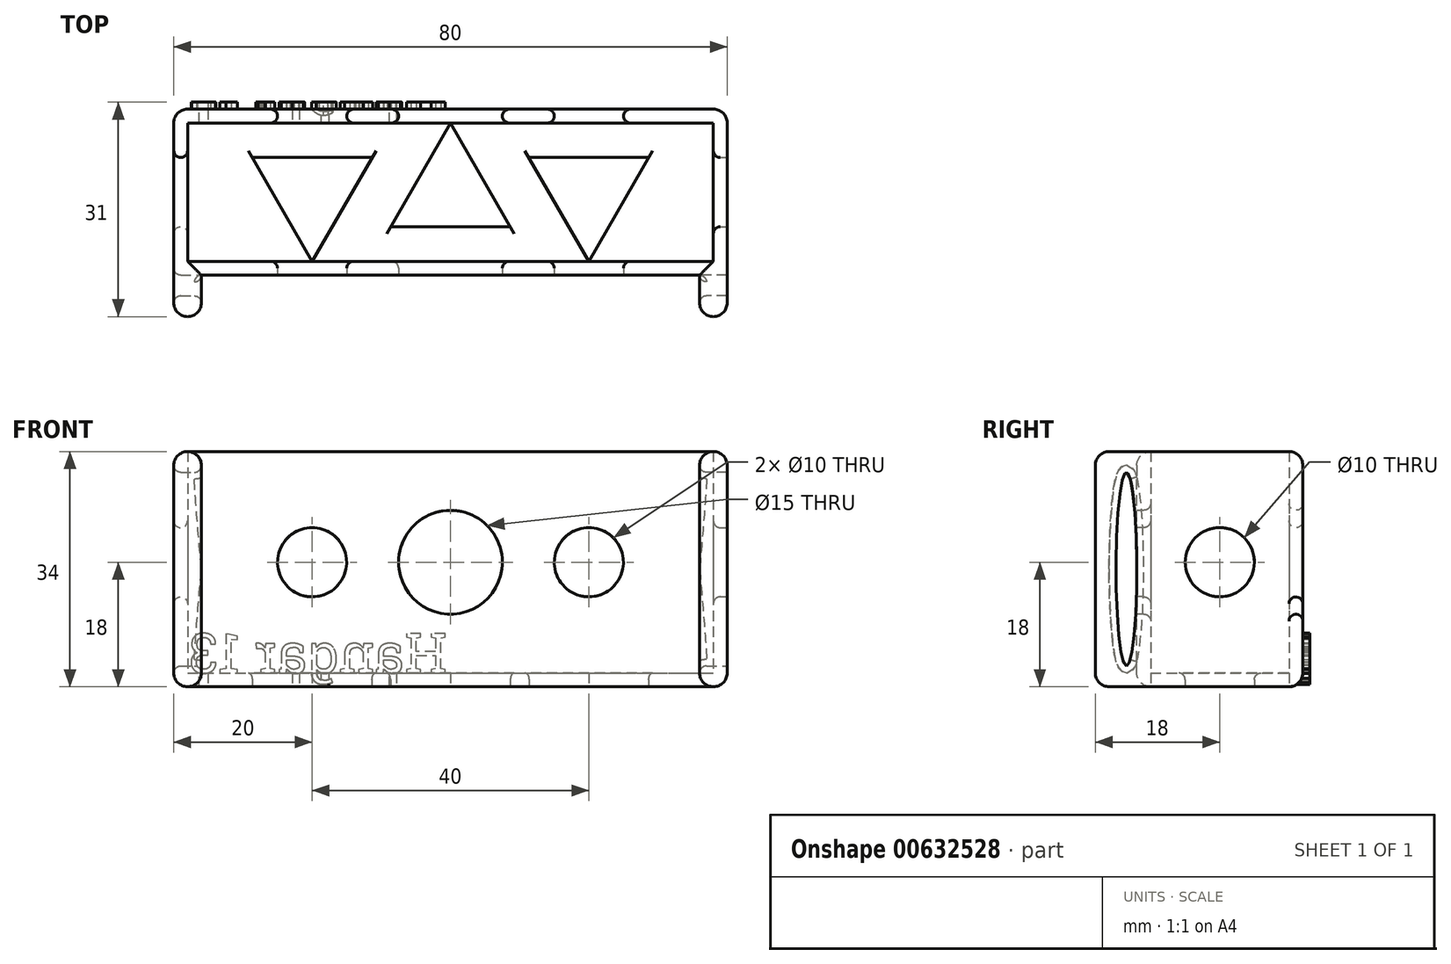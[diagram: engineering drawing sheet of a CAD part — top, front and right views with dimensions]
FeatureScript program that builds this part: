
annotation { "Feature Type Name" : "Feature", "Feature Type Description" : "" }
export const myFeature = defineFeature(function(context is Context, id is Id, definition is map)
    precondition{}
    {
        {
            var Q0;
            Q0=qCreatedBy(makeId("Top.planeOp"),FACE);
            var sketch = newSketch(context, id + "F0", { "sketchPlane" : qUnion([Q0])});
            skLineSegment(sketch, "E0.bottom", {"start": v(0, 0) * mm, "end": v(76, 0) * mm});
            skLineSegment(sketch, "E0.top", {"start": v(0, 20) * mm, "end": v(76, 20) * mm});
            skLineSegment(sketch, "E0.left", {"start": v(0, 0) * mm, "end": v(0, 20) * mm});
            skLineSegment(sketch, "E0.right", {"start": v(76, 0) * mm, "end": v(76, 20) * mm});
            skLineSegment(sketch, "E1.0", {"start": v(-2, -2) * mm, "end": v(78, -2) * mm});
            skLineSegment(sketch, "E1.1", {"start": v(-2, -2) * mm, "end": v(-2, 22) * mm});
            skLineSegment(sketch, "E1.2", {"start": v(-2, 22) * mm, "end": v(78, 22) * mm});
            skLineSegment(sketch, "E1.3", {"start": v(78, -2) * mm, "end": v(78, 22) * mm});
            skSolve(sketch);
        }
        {
            var Q0;
            Q0=makeQuery(id+"F0.imprint","IMPRINT",FACE,{"disambiguationData":[TD([[makeQuery(id+"F0.imprint","IMPRINT",EDGE,{"derivedFrom":sQuery(id+"F0.wireOp",EDGE,"E0.bottom")}),-1.0]])]});
            extrude(context, id + "F1", {"entities" : qUnion([Q0]), "depth" : 32 * mm, "offsetDistance" : 25 * mm});
        }
        {
            var Q0;
            Q0=makeQuery(id+"F1.opExtrude","SWEPT_FACE",FACE,{"disambiguationData":[OSD([sQuery(id+"F0.wireOp",EDGE,"E1.0")])]});
            var sketch = newSketch(context, id + "F2", { "sketchPlane" : qUnion([Q0])});
            skCircle(sketch, "E2", {"center": v(18, 16) * mm, "radius": 5 * mm});
            skCircle(sketch, "E3", {"center": v(38, 16) * mm, "radius": 7.5 * mm});
            skCircle(sketch, "E4", {"center": v(58, 16) * mm, "radius": 5 * mm});
            skSolve(sketch);
        }
        {
            var Q0;
            Q0=makeQuery(id+"F2.imprint","IMPRINT",FACE,{"disambiguationData":[TD([[makeQuery(id+"F2.imprint","IMPRINT",EDGE,{"derivedFrom":sQuery(id+"F2.wireOp",EDGE,"E3")}),1.0]])]});
            var Q1;
            Q1=makeQuery(id+"F2.imprint","IMPRINT",FACE,{"disambiguationData":[TD([[makeQuery(id+"F2.imprint","IMPRINT",EDGE,{"derivedFrom":sQuery(id+"F2.wireOp",EDGE,"E2")}),1.0]])]});
            var Q2;
            Q2=makeQuery(id+"F2.imprint","IMPRINT",FACE,{"disambiguationData":[TD([[makeQuery(id+"F2.imprint","IMPRINT",EDGE,{"derivedFrom":sQuery(id+"F2.wireOp",EDGE,"E4")}),1.0]])]});
            extrude(context, id + "F3", {"entities" : qUnion([Q0, Q1, Q2]), "operationType" : NewBodyOperationType.REMOVE, "oppositeDirection" : true, "depth" : 25 * mm, "offsetDistance" : 25 * mm});
        }
        {
            var Q0;
            Q0=makeQuery(id+"F1.opExtrude","SWEPT_FACE",FACE,{"disambiguationData":[OSD([sQuery(id+"F0.wireOp",EDGE,"E1.3")])]});
            var sketch = newSketch(context, id + "F4", { "sketchPlane" : qUnion([Q0])});
            skCircle(sketch, "E5", {"center": v(10, 16) * mm, "radius": 5 * mm});
            skSolve(sketch);
        }
        {
            var Q0;
            Q0=makeQuery(id+"F4.imprint","IMPRINT",FACE,{"disambiguationData":[TD([[makeQuery(id+"F4.imprint","IMPRINT",EDGE,{"derivedFrom":sQuery(id+"F4.wireOp",EDGE,"E5")}),1.0]])]});
            extrude(context, id + "F5", {"entities" : qUnion([Q0]), "operationType" : NewBodyOperationType.REMOVE, "oppositeDirection" : true, "depth" : 95 * mm, "offsetDistance" : 25 * mm});
        }
        {
            var Q0;
            Q0=makeQuery(id+"F1.opExtrude","CAP_FACE",FACE,{"disambiguationData":[OSD([sQuery(id+"F0.wireOp",EDGE,"E0.bottom"),sQuery(id+"F0.wireOp",EDGE,"E0.top"),sQuery(id+"F0.wireOp",EDGE,"E0.left"),sQuery(id+"F0.wireOp",EDGE,"E0.right"),sQuery(id+"F0.wireOp",EDGE,"E1.0"),sQuery(id+"F0.wireOp",EDGE,"E1.1"),sQuery(id+"F0.wireOp",EDGE,"E1.2"),sQuery(id+"F0.wireOp",EDGE,"E1.3")])],"isStart":true});
            var sketch = newSketch(context, id + "F6", { "sketchPlane" : qUnion([Q0])});
            skLineSegment(sketch, "E6.bottom", {"start": v(-2, 2) * mm, "end": v(78, 2) * mm});
            skLineSegment(sketch, "E6.top", {"start": v(-2, -22) * mm, "end": v(78, -22) * mm});
            skLineSegment(sketch, "E6.left", {"start": v(-2, 2) * mm, "end": v(-2, -22) * mm});
            skLineSegment(sketch, "E6.right", {"start": v(78, 2) * mm, "end": v(78, -22) * mm});
            skSolve(sketch);
        }
        {
            var Q0;
            Q0 = qSketchRegion(id + "F6", true);
            extrude(context, id + "F7", {"entities" : qUnion([Q0]), "operationType" : NewBodyOperationType.ADD, "depth" : 2 * mm, "offsetDistance" : 25 * mm});
        }
        {
            var Q0;
            Q0=makeQuery(id+"F7.boolean.opBoolean","MERGE",FACE,{"derivedFrom":[makeQuery(id+"F1.opExtrude","SWEPT_FACE",FACE,{"disambiguationData":[OSD([sQuery(id+"F0.wireOp",EDGE,"E1.0")])]}),makeQuery(id+"F7.opExtrude","SWEPT_FACE",FACE,{"disambiguationData":[OSD([sQuery(id+"F6.wireOp",EDGE,"E6.bottom")])]})]});
            var sketch = newSketch(context, id + "F8", { "sketchPlane" : qUnion([Q0])});
            skLineSegment(sketch, "E7.bottom", {"start": v(-2, -2) * mm, "end": v(2, -2) * mm});
            skLineSegment(sketch, "E7.top", {"start": v(-2, 32) * mm, "end": v(2, 32) * mm});
            skLineSegment(sketch, "E7.left", {"start": v(-2, -2) * mm, "end": v(-2, 32) * mm});
            skLineSegment(sketch, "E7.right", {"start": v(2, -2) * mm, "end": v(2, 32) * mm});
            skLineSegment(sketch, "E8.bottom", {"start": v(78, 32) * mm, "end": v(74, 32) * mm});
            skLineSegment(sketch, "E8.top", {"start": v(78, -2) * mm, "end": v(74, -2) * mm});
            skLineSegment(sketch, "E8.left", {"start": v(78, 32) * mm, "end": v(78, -2) * mm});
            skLineSegment(sketch, "E8.right", {"start": v(74, 32) * mm, "end": v(74, -2) * mm});
            skSolve(sketch);
        }
        {
            var Q0;
            Q0=makeQuery(id+"F8.imprint","IMPRINT",FACE,{"disambiguationData":[TD([[makeQuery(id+"F8.imprint","IMPRINT",EDGE,{"derivedFrom":sQuery(id+"F8.wireOp",EDGE,"E7.bottom")}),1.0]])]});
            var Q1;
            Q1=makeQuery(id+"F8.imprint","IMPRINT",FACE,{"disambiguationData":[TD([[makeQuery(id+"F8.imprint","IMPRINT",EDGE,{"derivedFrom":sQuery(id+"F8.wireOp",EDGE,"E8.bottom")}),-1.0]])]});
            extrude(context, id + "F9", {"entities" : qUnion([Q0, Q1]), "operationType" : NewBodyOperationType.ADD, "depth" : 6 * mm, "offsetDistance" : 25 * mm});
        }
        {
            var Q0;
            Q0=makeQuery(id+"F9.boolean.opBoolean","MERGE",FACE,{"derivedFrom":[makeQuery(id+"F7.boolean.opBoolean","MERGE",FACE,{"derivedFrom":[makeQuery(id+"F1.opExtrude","SWEPT_FACE",FACE,{"disambiguationData":[OSD([sQuery(id+"F0.wireOp",EDGE,"E1.3")])]}),makeQuery(id+"F7.opExtrude","SWEPT_FACE",FACE,{"disambiguationData":[OSD([sQuery(id+"F6.wireOp",EDGE,"E6.right")])]})]}),makeQuery(id+"F9.opExtrude","SWEPT_FACE",FACE,{"disambiguationData":[OSD([sQuery(id+"F8.wireOp",EDGE,"E8.left")])]})]});
            var sketch = newSketch(context, id + "F10", { "sketchPlane" : qUnion([Q0])});
            skLineSegment(sketch, "E9.bottom", {"start": v(-8, 32) * mm, "end": v(-2, 32) * mm});
            skLineSegment(sketch, "E9.top", {"start": v(-8, -2) * mm, "end": v(-2, -2) * mm});
            skLineSegment(sketch, "E9.left", {"start": v(-8, 32) * mm, "end": v(-8, -2) * mm});
            skEllipse(sketch, "E10", {"center": v(-3.5, 15) * mm, "majorRadius": 14 * mm, "minorRadius": 1.5 * mm, "majorAxis": v(0, -1)});
            skSolve(sketch);
        }
        {
            var Q0;
            Q0 = qSketchRegion(id + "F10", true);
            extrude(context, id + "F11", {"entities" : qUnion([Q0]), "operationType" : NewBodyOperationType.REMOVE, "oppositeDirection" : true, "depth" : 88.9 * mm, "offsetDistance" : 25 * mm});
        }
        {
            var Q0;
            Q0=makeQuery(id+"F9.boolean.opBoolean","MERGE",FACE,{"derivedFrom":[makeQuery(id+"F7.opExtrude","CAP_FACE",FACE,{"disambiguationData":[OSD([sQuery(id+"F6.wireOp",EDGE,"E6.bottom"),sQuery(id+"F6.wireOp",EDGE,"E6.top"),sQuery(id+"F6.wireOp",EDGE,"E6.left"),sQuery(id+"F6.wireOp",EDGE,"E6.right")])],"isStart":false}),makeQuery(id+"F9.opExtrude","SWEPT_FACE",FACE,{"disambiguationData":[OSD([sQuery(id+"F8.wireOp",EDGE,"E7.bottom")])]}),makeQuery(id+"F9.opExtrude","SWEPT_FACE",FACE,{"disambiguationData":[OSD([sQuery(id+"F8.wireOp",EDGE,"E8.top")])]})]});
            var sketch = newSketch(context, id + "F12", { "sketchPlane" : qUnion([Q0])});
            skCircle(sketch, "E11.cCircle", {"center": v(58, -10) * mm, "radius": 10 * mm, "construction": true});
            skPoint(sketch, "E11.cCircle.perimeterSnap0", {"position": v(58, -10) * mm});
            skLineSegment(sketch, "E11.0", {"start": v(58, 0) * mm, "end": v(66.66, -15) * mm});
            skPoint(sketch, "E11.0.startSnap0", {"position": v(58, -10) * mm});
            skLineSegment(sketch, "E11.1", {"start": v(66.66, -15) * mm, "end": v(49.34, -15) * mm});
            skLineSegment(sketch, "E11.2", {"start": v(49.34, -15) * mm, "end": v(58, 0) * mm});
            skCircle(sketch, "E12.cCircle", {"center": v(38, -10) * mm, "radius": 10 * mm, "construction": true});
            skLineSegment(sketch, "E12.0", {"start": v(38, -20) * mm, "end": v(29.34, -5) * mm});
            skLineSegment(sketch, "E12.1", {"start": v(29.34, -5) * mm, "end": v(46.66, -5) * mm});
            skLineSegment(sketch, "E12.2", {"start": v(46.66, -5) * mm, "end": v(38, -20) * mm});
            skCircle(sketch, "E13.cCircle", {"center": v(18, -10) * mm, "radius": 10 * mm, "construction": true});
            skPoint(sketch, "E13.cCircle.perimeterSnap0", {"position": v(18, -10) * mm});
            skLineSegment(sketch, "E13.0", {"start": v(18, 0) * mm, "end": v(26.66, -15) * mm});
            skPoint(sketch, "E13.0.startSnap0", {"position": v(18, -10) * mm});
            skLineSegment(sketch, "E13.1", {"start": v(26.66, -15) * mm, "end": v(9.34, -15) * mm});
            skLineSegment(sketch, "E13.2", {"start": v(9.34, -15) * mm, "end": v(18, 0) * mm});
            skSolve(sketch);
        }
        {
            var Q0;
            Q0=makeQuery(id+"F12.imprint","IMPRINT",FACE,{"disambiguationData":[TD([[makeQuery(id+"F12.imprint","IMPRINT",EDGE,{"derivedFrom":sQuery(id+"F12.wireOp",EDGE,"E12.0")}),-1.0]])]});
            var Q1;
            Q1=makeQuery(id+"F12.imprint","IMPRINT",FACE,{"disambiguationData":[TD([[makeQuery(id+"F12.imprint","IMPRINT",EDGE,{"derivedFrom":sQuery(id+"F12.wireOp",EDGE,"E11.0")}),-1.0]])]});
            var Q2;
            Q2=makeQuery(id+"F12.imprint","IMPRINT",FACE,{"disambiguationData":[TD([[makeQuery(id+"F12.imprint","IMPRINT",EDGE,{"derivedFrom":sQuery(id+"F12.wireOp",EDGE,"E13.0")}),-1.0]])]});
            extrude(context, id + "F13", {"entities" : qUnion([Q0, Q1, Q2]), "operationType" : NewBodyOperationType.REMOVE, "oppositeDirection" : true, "depth" : 25 * mm, "offsetDistance" : 25 * mm});
        }
        {
            var Q0;
            Q0=makeQuery(id+"F7.boolean.opBoolean","MERGE",FACE,{"derivedFrom":[makeQuery(id+"F1.opExtrude","SWEPT_FACE",FACE,{"disambiguationData":[OSD([sQuery(id+"F0.wireOp",EDGE,"E1.2")])]}),makeQuery(id+"F7.opExtrude","SWEPT_FACE",FACE,{"disambiguationData":[OSD([sQuery(id+"F6.wireOp",EDGE,"E6.top")])]})]});
            var sketch = newSketch(context, id + "F14", { "sketchPlane" : qUnion([Q0])});
            skText(sketch, "E14", { "text": "Hangar 13", "fontName": "RobotoSlab-Regular.ttf"});
            const initialGuessF14  = {"E14": [-0.0375, 0, 1, 0, 0.00574]};
            skSetInitialGuess(sketch, initialGuessF14);
            skSolve(sketch);
        }
        {
            var Q0;
            Q0 = qSketchRegion(id + "F14", true);
            extrude(context, id + "F15", {"entities" : qUnion([Q0]), "operationType" : NewBodyOperationType.ADD, "depth" : 1 * mm, "offsetDistance" : 25 * mm});
        }
        {
            var Q0;
            Q0=makeQuery(id+"F7.boolean.opBoolean","MERGE",EDGE,{"derivedFrom":[makeQuery(id+"F1.opExtrude","SWEPT_EDGE",EDGE,{"disambiguationData":[OSD([sQuery(id+"F0.wireOp",EDGE,"E1.1"),sQuery(id+"F0.wireOp",EDGE,"E1.2")])]}),makeQuery(id+"F7.opExtrude","SWEPT_EDGE",EDGE,{"disambiguationData":[OSD([sQuery(id+"F6.wireOp",EDGE,"E6.top"),sQuery(id+"F6.wireOp",EDGE,"E6.left")])]})]});
            var Q1;
            Q1=makeQuery(id+"F7.boolean.opBoolean","MERGE",EDGE,{"derivedFrom":[makeQuery(id+"F1.opExtrude","SWEPT_EDGE",EDGE,{"disambiguationData":[OSD([sQuery(id+"F0.wireOp",EDGE,"E1.2"),sQuery(id+"F0.wireOp",EDGE,"E1.3")])]}),makeQuery(id+"F7.opExtrude","SWEPT_EDGE",EDGE,{"disambiguationData":[OSD([sQuery(id+"F6.wireOp",EDGE,"E6.top"),sQuery(id+"F6.wireOp",EDGE,"E6.right")])]})]});
            var Q2;
            Q2=makeQuery(id+"F9.opExtrude","CAP_EDGE",EDGE,{"disambiguationData":[OSD([sQuery(id+"F8.wireOp",EDGE,"E7.left")])],"isStart":false});
            var Q3;
            Q3=makeQuery(id+"F9.opExtrude","CAP_EDGE",EDGE,{"disambiguationData":[OSD([sQuery(id+"F8.wireOp",EDGE,"E7.right")])],"isStart":false});
            var Q4;
            Q4=makeQuery(id+"F9.opExtrude","CAP_EDGE",EDGE,{"disambiguationData":[OSD([sQuery(id+"F8.wireOp",EDGE,"E8.right")])],"isStart":false});
            var Q5;
            Q5=makeQuery(id+"F9.opExtrude","CAP_EDGE",EDGE,{"disambiguationData":[OSD([sQuery(id+"F8.wireOp",EDGE,"E8.left")])],"isStart":false});
            fillet(context, id + "F16", {"entities" : qUnion([Q0, Q1, Q2, Q3, Q4, Q5]), "radius" : 2 * mm, "tangentPropagation" : true, "allowEdgeOverflow" : false});
        }
        {
            var Q0;
            Q0=makeQuery(id+"F1.opExtrude","CAP_EDGE",EDGE,{"disambiguationData":[OSD([sQuery(id+"F0.wireOp",EDGE,"E1.2")])],"isStart":false});
            var Q1;
            Q1=makeQuery(id+"F7.opExtrude","CAP_EDGE",EDGE,{"disambiguationData":[OSD([sQuery(id+"F6.wireOp",EDGE,"E6.top")])],"isStart":false});
            var Q2;
            Q2=makeQuery(id+"F7.opExtrude","CAP_EDGE",EDGE,{"disambiguationData":[OSD([sQuery(id+"F6.wireOp",EDGE,"E6.bottom")])],"isStart":false});
            var Q3;
            Q3=makeQuery(id+"F1.opExtrude","CAP_EDGE",EDGE,{"disambiguationData":[OSD([sQuery(id+"F0.wireOp",EDGE,"E1.0")])],"isStart":false});
            fillet(context, id + "F17", {"entities" : qUnion([Q0, Q1, Q2, Q3]), "radius" : 2 * mm, "tangentPropagation" : true, "allowEdgeOverflow" : false});
        }
        {
            var Q0;
            Q0=makeQuery(id+"F3.boolean.opBoolean","INTERSECT",EDGE,{"derivedFrom":[makeQuery(id+"F1.opExtrude","SWEPT_FACE",FACE,{"disambiguationData":[OSD([sQuery(id+"F0.wireOp",EDGE,"E1.2")])]}),makeQuery(id+"F3.opExtrude","SWEPT_FACE",FACE,{"disambiguationData":[OSD([sQuery(id+"F2.wireOp",EDGE,"E2")])]})]});
            var Q1;
            Q1=makeQuery(id+"F3.boolean.opBoolean","INTERSECT",EDGE,{"derivedFrom":[makeQuery(id+"F1.opExtrude","SWEPT_FACE",FACE,{"disambiguationData":[OSD([sQuery(id+"F0.wireOp",EDGE,"E1.2")])]}),makeQuery(id+"F3.opExtrude","SWEPT_FACE",FACE,{"disambiguationData":[OSD([sQuery(id+"F2.wireOp",EDGE,"E3")])]})]});
            var Q2;
            Q2=makeQuery(id+"F3.boolean.opBoolean","INTERSECT",EDGE,{"derivedFrom":[makeQuery(id+"F1.opExtrude","SWEPT_FACE",FACE,{"disambiguationData":[OSD([sQuery(id+"F0.wireOp",EDGE,"E1.2")])]}),makeQuery(id+"F3.opExtrude","SWEPT_FACE",FACE,{"disambiguationData":[OSD([sQuery(id+"F2.wireOp",EDGE,"E4")])]})]});
            var Q3;
            Q3=makeQuery(id+"F5.boolean.opBoolean","INTERSECT",EDGE,{"derivedFrom":[makeQuery(id+"F1.opExtrude","SWEPT_FACE",FACE,{"disambiguationData":[OSD([sQuery(id+"F0.wireOp",EDGE,"E1.1")])]}),makeQuery(id+"F5.opExtrude","SWEPT_FACE",FACE,{"disambiguationData":[OSD([sQuery(id+"F4.wireOp",EDGE,"E5")])]})]});
            var Q4;
            Q4=makeQuery(id+"F11.boolean.opBoolean","INTERSECT",EDGE,{"derivedFrom":[makeQuery(id+"F9.boolean.opBoolean","MERGE",FACE,{"derivedFrom":[makeQuery(id+"F7.boolean.opBoolean","MERGE",FACE,{"derivedFrom":[makeQuery(id+"F1.opExtrude","SWEPT_FACE",FACE,{"disambiguationData":[OSD([sQuery(id+"F0.wireOp",EDGE,"E1.1")])]}),makeQuery(id+"F7.opExtrude","SWEPT_FACE",FACE,{"disambiguationData":[OSD([sQuery(id+"F6.wireOp",EDGE,"E6.left")])]})]}),makeQuery(id+"F9.opExtrude","SWEPT_FACE",FACE,{"disambiguationData":[OSD([sQuery(id+"F8.wireOp",EDGE,"E7.left")])]})]}),makeQuery(id+"F11.opExtrude","SWEPT_FACE",FACE,{"disambiguationData":[OSD([sQuery(id+"F10.wireOp",EDGE,"E10")])]})]});
            var Q5;
            Q5=makeQuery(id+"F5.boolean.opBoolean","COPY",EDGE,{"derivedFrom":makeQuery(id+"F5.opExtrude","CAP_EDGE",EDGE,{"disambiguationData":[OSD([sQuery(id+"F4.wireOp",EDGE,"E5")])],"isStart":true})});
            var Q6;
            Q6=makeQuery(id+"F11.boolean.opBoolean","COPY",EDGE,{"derivedFrom":makeQuery(id+"F11.opExtrude","CAP_EDGE",EDGE,{"disambiguationData":[OSD([sQuery(id+"F10.wireOp",EDGE,"E10")])],"isStart":true})});
            var Q7;
            Q7=makeQuery(id+"F11.boolean.opBoolean","SPLIT",EDGE,{"disambiguationData":[OD(1.0)],"derivedFrom":makeQuery(id+"F3.boolean.opBoolean","COPY",EDGE,{"derivedFrom":makeQuery(id+"F3.opExtrude","CAP_EDGE",EDGE,{"disambiguationData":[OSD([sQuery(id+"F2.wireOp",EDGE,"E4")])],"isStart":true})})});
            var Q8;
            Q8=makeQuery(id+"F11.boolean.opBoolean","SPLIT",EDGE,{"disambiguationData":[OD(1.0)],"derivedFrom":makeQuery(id+"F3.boolean.opBoolean","COPY",EDGE,{"derivedFrom":makeQuery(id+"F3.opExtrude","CAP_EDGE",EDGE,{"disambiguationData":[OSD([sQuery(id+"F2.wireOp",EDGE,"E3")])],"isStart":true})})});
            var Q9;
            Q9=makeQuery(id+"F11.boolean.opBoolean","SPLIT",EDGE,{"disambiguationData":[OD(1.0)],"derivedFrom":makeQuery(id+"F3.boolean.opBoolean","COPY",EDGE,{"derivedFrom":makeQuery(id+"F3.opExtrude","CAP_EDGE",EDGE,{"disambiguationData":[OSD([sQuery(id+"F2.wireOp",EDGE,"E2")])],"isStart":true})})});
            fillet(context, id + "F18", {"entities" : qUnion([Q0, Q1, Q2, Q3, Q4, Q5, Q6, Q7, Q8, Q9]), "radius" : 1 * mm, "tangentPropagation" : true, "allowEdgeOverflow" : false});
        }
        {
            var Q0;
            Q0=makeQuery(id+"F3.boolean.opBoolean","INTERSECT",EDGE,{"derivedFrom":[makeQuery(id+"F1.opExtrude","SWEPT_FACE",FACE,{"disambiguationData":[OSD([sQuery(id+"F0.wireOp",EDGE,"E0.top")])]}),makeQuery(id+"F3.opExtrude","SWEPT_FACE",FACE,{"disambiguationData":[OSD([sQuery(id+"F2.wireOp",EDGE,"E4")])]})]});
            var Q1;
            Q1=makeQuery(id+"F3.boolean.opBoolean","INTERSECT",EDGE,{"derivedFrom":[makeQuery(id+"F1.opExtrude","SWEPT_FACE",FACE,{"disambiguationData":[OSD([sQuery(id+"F0.wireOp",EDGE,"E0.top")])]}),makeQuery(id+"F3.opExtrude","SWEPT_FACE",FACE,{"disambiguationData":[OSD([sQuery(id+"F2.wireOp",EDGE,"E3")])]})]});
            var Q2;
            Q2=makeQuery(id+"F3.boolean.opBoolean","INTERSECT",EDGE,{"derivedFrom":[makeQuery(id+"F1.opExtrude","SWEPT_FACE",FACE,{"disambiguationData":[OSD([sQuery(id+"F0.wireOp",EDGE,"E0.top")])]}),makeQuery(id+"F3.opExtrude","SWEPT_FACE",FACE,{"disambiguationData":[OSD([sQuery(id+"F2.wireOp",EDGE,"E2")])]})]});
            var Q3;
            Q3=makeQuery(id+"F3.boolean.opBoolean","INTERSECT",EDGE,{"derivedFrom":[makeQuery(id+"F1.opExtrude","SWEPT_FACE",FACE,{"disambiguationData":[OSD([sQuery(id+"F0.wireOp",EDGE,"E0.bottom")])]}),makeQuery(id+"F3.opExtrude","SWEPT_FACE",FACE,{"disambiguationData":[OSD([sQuery(id+"F2.wireOp",EDGE,"E4")])]})]});
            var Q4;
            Q4=makeQuery(id+"F3.boolean.opBoolean","INTERSECT",EDGE,{"derivedFrom":[makeQuery(id+"F1.opExtrude","SWEPT_FACE",FACE,{"disambiguationData":[OSD([sQuery(id+"F0.wireOp",EDGE,"E0.bottom")])]}),makeQuery(id+"F3.opExtrude","SWEPT_FACE",FACE,{"disambiguationData":[OSD([sQuery(id+"F2.wireOp",EDGE,"E3")])]})]});
            var Q5;
            Q5=makeQuery(id+"F3.boolean.opBoolean","INTERSECT",EDGE,{"derivedFrom":[makeQuery(id+"F1.opExtrude","SWEPT_FACE",FACE,{"disambiguationData":[OSD([sQuery(id+"F0.wireOp",EDGE,"E0.bottom")])]}),makeQuery(id+"F3.opExtrude","SWEPT_FACE",FACE,{"disambiguationData":[OSD([sQuery(id+"F2.wireOp",EDGE,"E2")])]})]});
            var Q6;
            Q6=makeQuery(id+"F5.boolean.opBoolean","INTERSECT",EDGE,{"derivedFrom":[makeQuery(id+"F1.opExtrude","SWEPT_FACE",FACE,{"disambiguationData":[OSD([sQuery(id+"F0.wireOp",EDGE,"E0.left")])]}),makeQuery(id+"F5.opExtrude","SWEPT_FACE",FACE,{"disambiguationData":[OSD([sQuery(id+"F4.wireOp",EDGE,"E5")])]})]});
            var Q7;
            Q7=makeQuery(id+"F5.boolean.opBoolean","INTERSECT",EDGE,{"derivedFrom":[makeQuery(id+"F1.opExtrude","SWEPT_FACE",FACE,{"disambiguationData":[OSD([sQuery(id+"F0.wireOp",EDGE,"E0.right")])]}),makeQuery(id+"F5.opExtrude","SWEPT_FACE",FACE,{"disambiguationData":[OSD([sQuery(id+"F4.wireOp",EDGE,"E5")])]})]});
            var Q8;
            Q8=makeQuery(id+"F11.boolean.opBoolean","INTERSECT",EDGE,{"derivedFrom":[makeQuery(id+"F9.opExtrude","SWEPT_FACE",FACE,{"disambiguationData":[OSD([sQuery(id+"F8.wireOp",EDGE,"E8.right")])]}),makeQuery(id+"F11.opExtrude","SWEPT_FACE",FACE,{"disambiguationData":[OSD([sQuery(id+"F10.wireOp",EDGE,"E10")])]})]});
            var Q9;
            Q9=makeQuery(id+"F11.boolean.opBoolean","INTERSECT",EDGE,{"derivedFrom":[makeQuery(id+"F9.opExtrude","SWEPT_FACE",FACE,{"disambiguationData":[OSD([sQuery(id+"F8.wireOp",EDGE,"E7.right")])]}),makeQuery(id+"F11.opExtrude","SWEPT_FACE",FACE,{"disambiguationData":[OSD([sQuery(id+"F10.wireOp",EDGE,"E10")])]})]});
            fillet(context, id + "F19", {"entities" : qUnion([Q0, Q1, Q2, Q3, Q4, Q5, Q6, Q7, Q8, Q9]), "radius" : 1 * mm, "tangentPropagation" : true, "allowEdgeOverflow" : false});
        }
        {
            var Q0;
            Q0=makeQuery(id+"F13.boolean.opBoolean","INTERSECT",EDGE,{"derivedFrom":[makeQuery(id+"F7.opExtrude","CAP_FACE",FACE,{"disambiguationData":[OSD([sQuery(id+"F6.wireOp",EDGE,"E6.bottom"),sQuery(id+"F6.wireOp",EDGE,"E6.top"),sQuery(id+"F6.wireOp",EDGE,"E6.left"),sQuery(id+"F6.wireOp",EDGE,"E6.right")])],"isStart":true}),makeQuery(id+"F13.opExtrude","SWEPT_FACE",FACE,{"disambiguationData":[OSD([sQuery(id+"F12.wireOp",EDGE,"E11.1")])]})]});
            var Q1;
            Q1=makeQuery(id+"F13.boolean.opBoolean","INTERSECT",EDGE,{"derivedFrom":[makeQuery(id+"F7.opExtrude","CAP_FACE",FACE,{"disambiguationData":[OSD([sQuery(id+"F6.wireOp",EDGE,"E6.bottom"),sQuery(id+"F6.wireOp",EDGE,"E6.top"),sQuery(id+"F6.wireOp",EDGE,"E6.left"),sQuery(id+"F6.wireOp",EDGE,"E6.right")])],"isStart":true}),makeQuery(id+"F13.opExtrude","SWEPT_FACE",FACE,{"disambiguationData":[OSD([sQuery(id+"F12.wireOp",EDGE,"E12.1")])]})]});
            var Q2;
            Q2=makeQuery(id+"F13.boolean.opBoolean","INTERSECT",EDGE,{"derivedFrom":[makeQuery(id+"F7.opExtrude","CAP_FACE",FACE,{"disambiguationData":[OSD([sQuery(id+"F6.wireOp",EDGE,"E6.bottom"),sQuery(id+"F6.wireOp",EDGE,"E6.top"),sQuery(id+"F6.wireOp",EDGE,"E6.left"),sQuery(id+"F6.wireOp",EDGE,"E6.right")])],"isStart":true}),makeQuery(id+"F13.opExtrude","SWEPT_FACE",FACE,{"disambiguationData":[OSD([sQuery(id+"F12.wireOp",EDGE,"E13.1")])]})]});
            var Q3;
            Q3=makeQuery(id+"F13.boolean.opBoolean","COPY",EDGE,{"derivedFrom":makeQuery(id+"F13.opExtrude","CAP_EDGE",EDGE,{"disambiguationData":[OSD([sQuery(id+"F12.wireOp",EDGE,"E11.1")])],"isStart":true})});
            var Q4;
            Q4=makeQuery(id+"F13.boolean.opBoolean","COPY",EDGE,{"derivedFrom":makeQuery(id+"F13.opExtrude","CAP_EDGE",EDGE,{"disambiguationData":[OSD([sQuery(id+"F12.wireOp",EDGE,"E13.1")])],"isStart":true})});
            var Q5;
            Q5=makeQuery(id+"F13.boolean.opBoolean","COPY",EDGE,{"derivedFrom":makeQuery(id+"F13.opExtrude","CAP_EDGE",EDGE,{"disambiguationData":[OSD([sQuery(id+"F12.wireOp",EDGE,"E12.1")])],"isStart":true})});
            fillet(context, id + "F20", {"entities" : qUnion([Q0, Q1, Q2, Q3, Q4, Q5]), "radius" : 1 * mm, "tangentPropagation" : true, "allowEdgeOverflow" : false});
        }
    });
